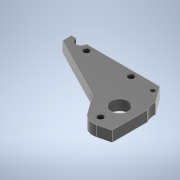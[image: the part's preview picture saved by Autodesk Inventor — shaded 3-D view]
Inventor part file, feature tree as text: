
AUTODESK INVENTOR PART (.ipt)
format: ipt  version: 2022 (Build 260153000, 153)  size: 136,192 bytes
history: native  units: mm
features: extrude x1, fillet x1, sketch x1
ambient origin geometry x8: Origin, YZ Plane, XZ Plane, XY Plane, X Axis, Y Axis, Z Axis, Center Point
bodies: Solid1 (feature_tree)
feature tree (3):
  extrude  "Extrusion1"  Depth=7.5mm
  fillet  "Fillet1"  Radius=12.0mm
  sketch  "Sketch1"  dims[d2=50.0mm d6=11.0mm d7=12.0mm d8=20.0mm d15=3.5mm d16=17.0mm d17=10.0mm d23=2.5mm d26=3.5mm d28=2.5mm d30=3.0mm d31=6.0mm d32=0.0mm d33=7.5mm]
